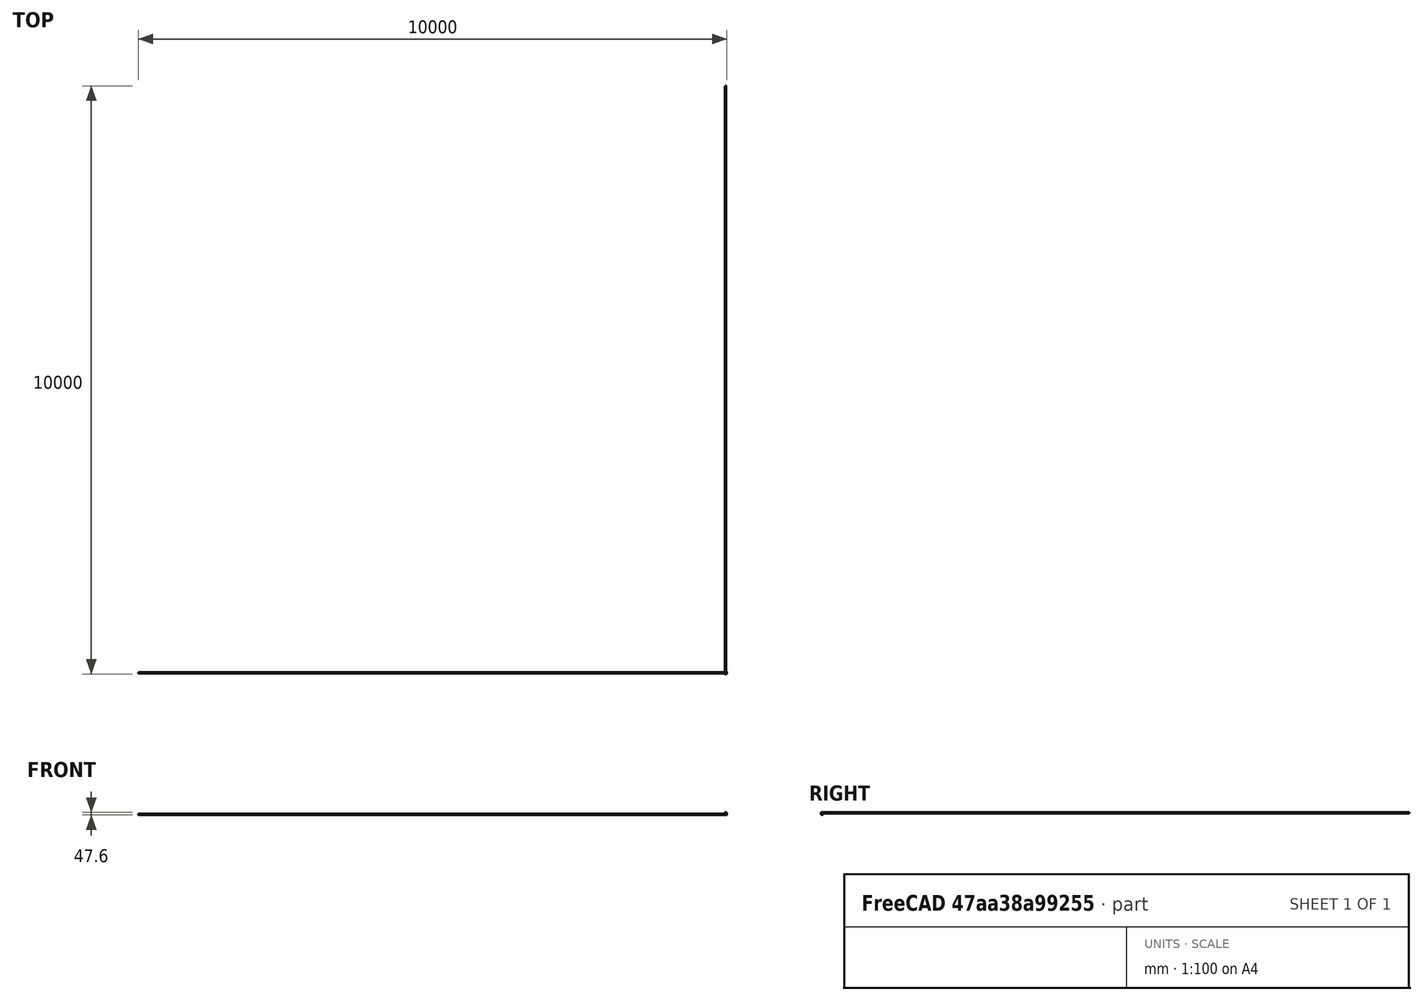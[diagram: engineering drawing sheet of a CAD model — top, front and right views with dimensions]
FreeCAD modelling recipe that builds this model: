
FCSTD DOCUMENT  (FreeCAD 0.16R)
Label: FlashLightClampOffset1
License: All rights reserved
LicenseURL: http://en.wikipedia.org/wiki/All_rights_reserved
objects: Sketcher::SketchObject×4, PartDesign::Pocket×3, PartDesign::Fillet×2, PartDesign::Pad×1, PartDesign::Chamfer×1, Mesh::Feature×1
note: 15 computed .brp shape members not serialized (recipe doc carries the construction recipe); baked Part::Feature solids carry a one-line shape summary decoded from their .brp

FEATURE [Sketcher::SketchObject] Sketch
  sketch-geometry (4):
    g0: LineSegment StartX=-20 StartY=20 StartZ=0 EndX=20 EndY=20 EndZ=0
    g1: LineSegment StartX=20 StartY=20 StartZ=0 EndX=20 EndY=-20 EndZ=0
    g2: LineSegment StartX=20 StartY=-20 StartZ=0 EndX=-20 EndY=-20 EndZ=0
    g3: LineSegment StartX=-20 StartY=-20 StartZ=0 EndX=-20 EndY=20 EndZ=0
  constraints (11):
    c: Coincident(g0,g1)
    c: Coincident(g1,g2)
    c: Coincident(g2,g3)
    c: Coincident(g3,g0)
    c: Horizontal(g0)
    c: Horizontal(g2)
    c: Vertical(g1)
    c: Vertical(g3)
    c: Symmetric(g0,g1,g-1)
    c: Distance(g0) = 40
    c: Distance(g1) = 40
FEATURE [PartDesign::Pad] Pad
  Length = 37
  Length2 = 100
  Sketch = -> Sketch
  Type = 0
FEATURE [Sketcher::SketchObject] Sketch001
  Placement = pos=(20,0,0) rot=(0.57735,0.57735,0.57735;2.0944rad)
  Support = -> Pad [Face2]
  sketch-geometry (1):
    g0: Circle CenterX=0 CenterY=4 CenterZ=0 NormalX=0 NormalY=0 NormalZ=1 Radius=10.5
  constraints (3):
    c: Radius(g0) = 10.5
    c: PointOnObject(g0,g-2)
    c: DistanceY(g0) = 4
FEATURE [PartDesign::Pocket] Pocket
  Length = 5
  Sketch = -> Sketch001
  Type = 1
FEATURE [Sketcher::SketchObject] Sketch002
  Placement = pos=(0,-20,0) rot=(1,0,0;1.5708rad)
  Support = -> Pocket [Face9]
  sketch-geometry (1):
    g0: Circle CenterX=0 CenterY=30 CenterZ=0 NormalX=0 NormalY=0 NormalZ=1 Radius=11.1
  constraints (3):
    c: Radius(g0) = 11.1
    c: PointOnObject(g0,g-2)
    c: DistanceY(g0) = 30
FEATURE [PartDesign::Pocket] Pocket001
  Length = 5
  Sketch = -> Sketch002
  Type = 1
FEATURE [Sketcher::SketchObject] Sketch003
  Placement = pos=(20,0,0) rot=(0.57735,0.57735,0.57735;2.0944rad)
  Support = -> Pocket001 [Face3]
  sketch-geometry (1):
    g0: Circle CenterX=0 CenterY=4 CenterZ=0 NormalX=0 NormalY=0 NormalZ=1 Radius=17
  constraints (3):
    c: Radius(g0) = 17
    c: PointOnObject(g0,g-2)
    c: DistanceY(g0) = 4
FEATURE [PartDesign::Pocket] Pocket002
  Length = 13
  Sketch = -> Sketch003
  Type = 0
FEATURE [PartDesign::Fillet] Fillet
  Base = -> Pocket002 [Edge18,Edge22]
  Radius = 3
FEATURE [PartDesign::Fillet] Fillet001
  Base = -> Fillet [Edge22,Edge42]
  Radius = 1
FEATURE [PartDesign::Chamfer] Chamfer
  Base = -> Fillet001 [Edge41,Edge42,Edge20,Edge43,Edge40,Edge44,Edge27,Edge45,Edge46,Edge5,Edge17,Edge25,Edge26,Edge28,Edge29,Edge30,Edge31,Edge32,Edge6,Edge33,Edge24,Edge34,Edge35,Edge18,Edge19,Edge21,Edge22,Edge23,Edge14,Edge4]
  Size = 1
FEATURE [Mesh::Feature] Mesh  label="Chamfer (Meshed)"
